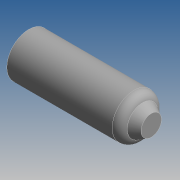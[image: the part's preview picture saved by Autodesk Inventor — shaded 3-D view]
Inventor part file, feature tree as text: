
AUTODESK INVENTOR PART (.ipt)
format: ipt  version: 2015 SP1 (Build 190203100, 203)  size: 206,336 bytes
history: native  units: mm
features: revolve x1, fillet x1, sketch x1
ambient origin geometry x8: Origin, YZ Plane, XZ Plane, XY Plane, X Axis, Y Axis, Z Axis, Center Point
bodies: Solid1 (feature_tree)
feature tree (3):
  revolve  "Revolution1"  [1 undecoded]
  fillet  "Fillet2"  Radius=14.0mm
  sketch  "Sketch1"  dims[d0=5.0mm d1=3.5mm d3=14.0mm d4=90.0deg d6=2.0mm d7=60.0deg d8=1.0mm d9=1.0mm]
note: 1 required parameter value undecoded (feature->parameter linkage not recoverable at this tier; creation-order binding heuristic only, values carry confidence <= 0.55)
